# Revit family: Accessory-Towel_Ring-KOHLER-Archer-K-11057
name_source: partatom
category: Specialty Equipment
revit_build: Autodesk Revit 2015 (Build: 20140606_1530(x64)
units: mm (PartAtom-declared; Revit-internal decimal feet)

## types (2) — shared parameters
ADA Compliant = No
Assembly Code = C1030200
Date Modified = 11/16/2018
Default Elevation = 42"
Description = Towel ring
Height = 8 1/8"
Length = 7"
Manufacturer = KOHLER Co.
MasterFormat 1995 = 10820
MasterFormat 2004 = 10.28.13
Material = Premum Metal Construction
Product Documentation Link = http://www.us.kohler.com
Product Name = Archer
Product Page URL = http://www.us.kohler.com
URL = https://www.us.kohler.com
Width = 4 1/4"

## per-type parameters (varying)
| type | Finish | Model | Type |
| CP-Polished Chrome | Kohler-Metal-CP-Polished_Chrome | K-11057-CP | 1 |
| BN-Vibrant Brushed Nickel | Kohler-Metal-BN-Vibrant_Brushed_Nickel | K-11057-BN | 2 |

## geometry (parser evidence)
native form markers: Sweep x6
no freeform markers — native parametric forms only
